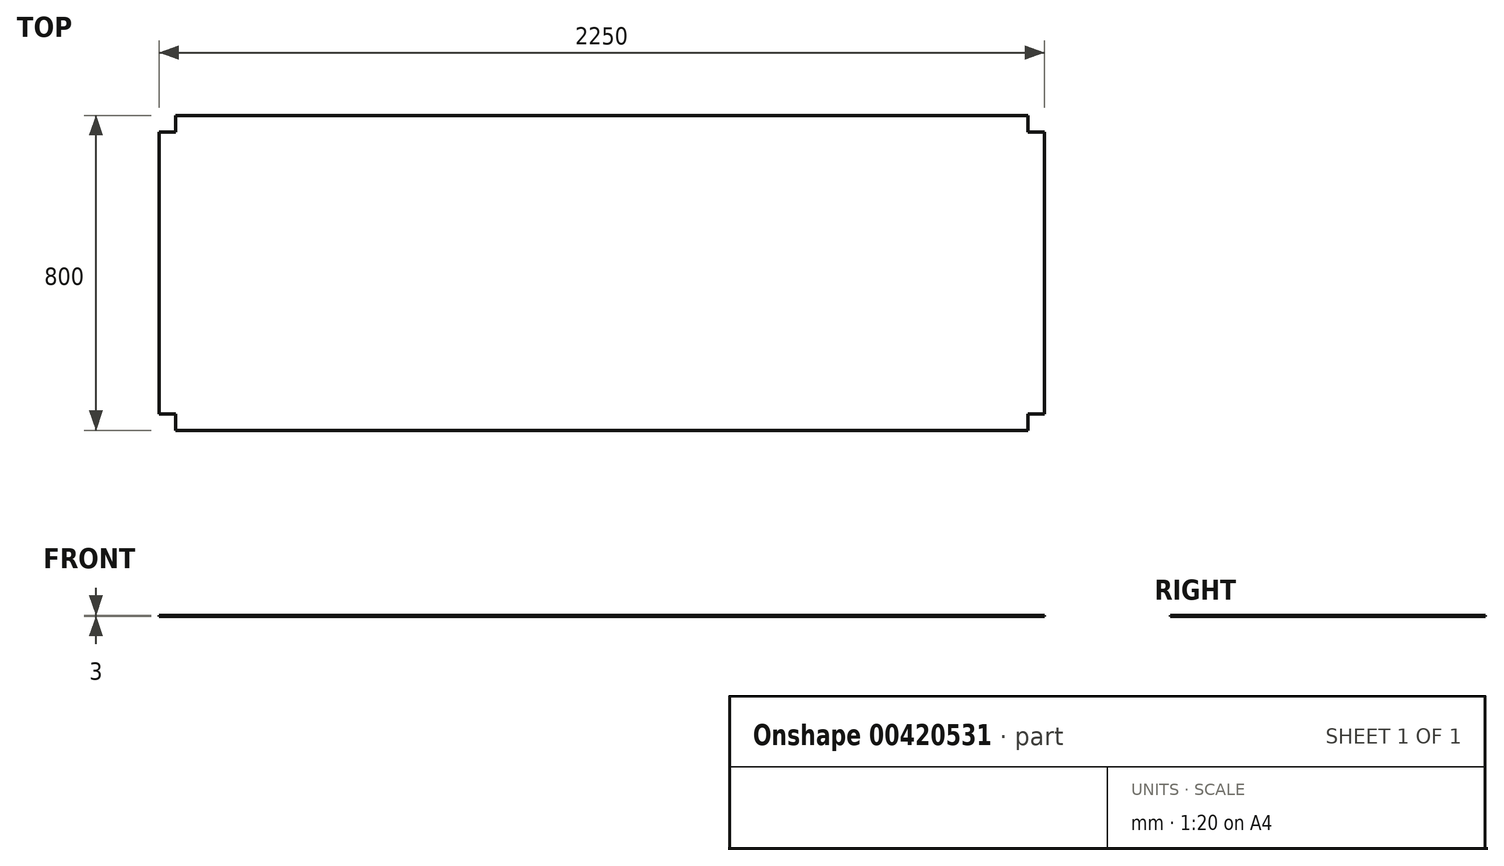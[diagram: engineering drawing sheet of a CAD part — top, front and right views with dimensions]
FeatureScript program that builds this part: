
annotation { "Feature Type Name" : "Feature", "Feature Type Description" : "" }
export const myFeature = defineFeature(function(context is Context, id is Id, definition is map)
    precondition{}
    {
        {
            var Q0;
            Q0=qCreatedBy(makeId("Top.planeOp"),FACE);
            var sketch = newSketch(context, id + "F0", { "sketchPlane" : qUnion([Q0])});
            skLineSegment(sketch, "E0.bottom", {"start": v(-1107.08, 213.13) * mm, "end": v(1058.92, 213.13) * mm});
            skLineSegment(sketch, "E0.top", {"start": v(-1107.08, -586.87) * mm, "end": v(1058.92, -586.87) * mm});
            skLineSegment(sketch, "E0.left", {"start": v(-1149.08, 171.13) * mm, "end": v(-1149.08, -544.87) * mm});
            skLineSegment(sketch, "E0.right", {"start": v(1100.92, 171.13) * mm, "end": v(1100.92, -544.87) * mm});
            skLineSegment(sketch, "E1.top", {"start": v(-1149.08, 171.13) * mm, "end": v(-1107.08, 171.13) * mm});
            skLineSegment(sketch, "E1.right", {"start": v(-1107.08, 213.13) * mm, "end": v(-1107.08, 171.13) * mm});
            skPoint(sketch, "E2", {"position": v(-24.08, 213.13) * mm});
            skPoint(sketch, "E3", {"position": v(-24.08, -586.87) * mm});
            skLineSegment(sketch, "E4", {"start": v(-24.08, 213.13) * mm, "end": v(-24.08, -586.87) * mm, "construction": true});
            skPoint(sketch, "E5", {"position": v(-1149.08, -186.87) * mm});
            skPoint(sketch, "E6", {"position": v(1100.92, -186.87) * mm});
            skLineSegment(sketch, "E7", {"start": v(-1149.08, -186.87) * mm, "end": v(1100.92, -186.87) * mm, "construction": true});
            skLineSegment(sketch, "E8.MirrorCS", {"start": v(1058.92, 213.13) * mm, "end": v(1058.92, 171.13) * mm});
            skLineSegment(sketch, "E9.MirrorCS", {"start": v(1100.92, 171.13) * mm, "end": v(1058.92, 171.13) * mm});
            skLineSegment(sketch, "E10.MirrorCS", {"start": v(-1149.08, -544.87) * mm, "end": v(-1107.08, -544.87) * mm});
            skLineSegment(sketch, "E11.MirrorCS", {"start": v(-1107.08, -586.87) * mm, "end": v(-1107.08, -544.87) * mm});
            skLineSegment(sketch, "E12.MirrorCS", {"start": v(1100.92, -544.87) * mm, "end": v(1058.92, -544.87) * mm});
            skLineSegment(sketch, "E13.MirrorCS", {"start": v(1058.92, -586.87) * mm, "end": v(1058.92, -544.87) * mm});
            skPoint(sketch, "E14.orphan", {"position": v(-1149.08, 213.13) * mm});
            skPoint(sketch, "E15.orphan", {"position": v(-1149.08, -586.87) * mm});
            skPoint(sketch, "E16.orphan", {"position": v(1100.92, -586.87) * mm});
            skPoint(sketch, "E17.orphan", {"position": v(1100.92, 213.13) * mm});
            skSolve(sketch);
        }
        {
            var Q0;
            Q0 = qSketchRegion(id + "F0", true);
            extrude(context, id + "F1", {"entities" : qUnion([Q0]), "depth" : 3 * mm});
        }
    });
